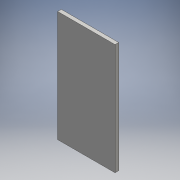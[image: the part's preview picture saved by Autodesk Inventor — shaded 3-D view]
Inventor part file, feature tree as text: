
AUTODESK INVENTOR PART (.ipt)
format: ipt  version: 2016 SP1 (Build 200210100, 210)  size: 107,008 bytes
history: native  units: mm
features: extrude x2, sketch x2, other x1
ambient origin geometry x8: Origin, YZ Plane, XZ Plane, XY Plane, X Axis, Y Axis, Z Axis, Center Point
bodies: Body1 (feature_tree)
feature tree (5):
  other  "Bryła1"
  extrude  "Wyciągnięcie proste1"  Depth=23.5mm
  extrude  "Wyciągnięcie proste2"  Depth=45.5mm
  sketch  "Szkic1"
  sketch  "Szkic2"
